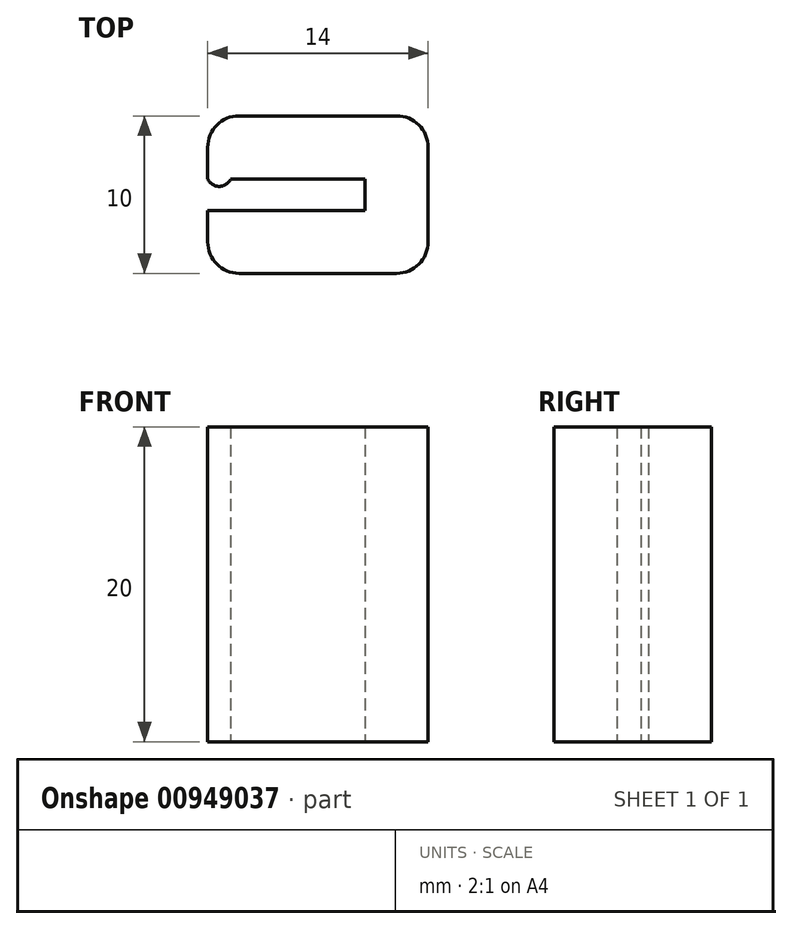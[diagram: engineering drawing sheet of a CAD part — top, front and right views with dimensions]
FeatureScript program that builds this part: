
annotation { "Feature Type Name" : "Feature", "Feature Type Description" : "" }
export const myFeature = defineFeature(function(context is Context, id is Id, definition is map)
    precondition{}
    {
        {
            var Q0;
            Q0=qCreatedBy(makeId("Top.planeOp"),FACE);
            var sketch = newSketch(context, id + "F0", { "sketchPlane" : qUnion([Q0])});
            skLineSegment(sketch, "E0.bottom", {"start": v(5, 1) * mm, "end": v(-5, 1) * mm});
            skLineSegment(sketch, "E0.top", {"start": v(5, -1) * mm, "end": v(-5, -1) * mm});
            skLineSegment(sketch, "E0.left", {"start": v(5, 1) * mm, "end": v(5, -1) * mm});
            skPoint(sketch, "E0.middle", {"position": v(0, 0) * mm});
            skLineSegment(sketch, "E1.bottom", {"start": v(-5, 1) * mm, "end": v(5, 1) * mm});
            skLineSegment(sketch, "E1.top", {"start": v(-5, 5) * mm, "end": v(5, 5) * mm});
            skLineSegment(sketch, "E1.left", {"start": v(-5, 1) * mm, "end": v(-5, 5) * mm});
            skLineSegment(sketch, "E1.right", {"start": v(5, 1) * mm, "end": v(5, 5) * mm});
            skLineSegment(sketch, "E2.top", {"start": v(5, -5) * mm, "end": v(-5, -5) * mm});
            skLineSegment(sketch, "E2.left", {"start": v(5, -1) * mm, "end": v(5, -5) * mm});
            skLineSegment(sketch, "E2.right", {"start": v(-5, -1) * mm, "end": v(-5, -5) * mm});
            skLineSegment(sketch, "E3.bottom", {"start": v(5, 5) * mm, "end": v(9, 5) * mm});
            skLineSegment(sketch, "E3.top", {"start": v(5, -5) * mm, "end": v(9, -5) * mm});
            skLineSegment(sketch, "E3.left", {"start": v(5, 5) * mm, "end": v(5, -5) * mm});
            skLineSegment(sketch, "E3.right", {"start": v(9, 5) * mm, "end": v(9, -5) * mm});
            skArc(sketch, "E4", {"start": v(-5, 1) * mm, "mid": v(-4.27, 0.52) * mm, "end": v(-3.53, 1) * mm});
            skLineSegment(sketch, "E5", {"start": v(0, 0) * mm, "end": v(-27.66, 0) * mm, "construction": true});
            skArc(sketch, "E6.MirrorCS", {"start": v(-5, -1) * mm, "mid": v(-4.27, -0.52) * mm, "end": v(-3.53, -1) * mm});
            skSolve(sketch);
        }
        {
            var Q0;
            Q0=makeQuery(id+"F0.imprint","IMPRINT",FACE,{"disambiguationData":[TD([[makeQuery(id+"F0.imprint","IMPRINT",EDGE,{"derivedFrom":sQuery(id+"F0.wireOp",EDGE,"E0.left")}),1.0]])]});
            var Q1;
            Q1=makeQuery(id+"F0.imprint","IMPRINT",FACE,{"disambiguationData":[TD([[makeQuery(id+"F0.imprint","IMPRINT",EDGE,{"derivedFrom":sQuery(id+"F0.wireOp",EDGE,"E1.top")}),-1.0]])]});
            var Q2;
            Q2=makeQuery(id+"F0.imprint","IMPRINT",FACE,{"disambiguationData":[TD([[makeQuery(id+"F0.imprint","IMPRINT",EDGE,{"derivedFrom":sQuery(id+"F0.wireOp",EDGE,"E2.top")}),-1.0]])]});
            var Q3;
            {var subQ0=sQuery(id+"F0.wireOp",EDGE,"E6.MirrorCS");Q3=makeQuery(id+"F0.imprint","IMPRINT",FACE,{"disambiguationData":[TD([[makeQuery(id+"F0.imprint","IMPRINT",EDGE,{"derivedFrom":subQ0}),-1.0]])]});}
            var Q4;
            {var subQ0=sQuery(id+"F0.wireOp",EDGE,"E4");Q4=makeQuery(id+"F0.imprint","IMPRINT",FACE,{"disambiguationData":[TD([[makeQuery(id+"F0.imprint","IMPRINT",EDGE,{"derivedFrom":subQ0}),1.0]])]});}
            extrude(context, id + "F1", {"entities" : qUnion([Q0, Q1, Q2, Q3, Q4]), "depth" : 20 * mm, "offsetDistance" : 25 * mm});
        }
        {
            var Q0;
            Q0=makeQuery(id+"F1.opExtrude","SWEPT_EDGE",EDGE,{"disambiguationData":[OSD([sQuery(id+"F0.wireOp",EDGE,"E3.bottom"),sQuery(id+"F0.wireOp",EDGE,"E3.right")])]});
            var Q1;
            Q1=makeQuery(id+"F1.opExtrude","SWEPT_EDGE",EDGE,{"disambiguationData":[OSD([sQuery(id+"F0.wireOp",EDGE,"E3.top"),sQuery(id+"F0.wireOp",EDGE,"E3.right")])]});
            var Q2;
            Q2=makeQuery(id+"F1.opExtrude","SWEPT_EDGE",EDGE,{"disambiguationData":[OSD([sQuery(id+"F0.wireOp",EDGE,"E2.top"),sQuery(id+"F0.wireOp",EDGE,"E2.right")])]});
            var Q3;
            Q3=makeQuery(id+"F1.opExtrude","SWEPT_EDGE",EDGE,{"disambiguationData":[OSD([sQuery(id+"F0.wireOp",EDGE,"E1.top"),sQuery(id+"F0.wireOp",EDGE,"E1.left")])]});
            fillet(context, id + "F2", {"entities" : qUnion([Q0, Q1, Q2, Q3]), "tangentPropagation" : true, "radius" : 2 * mm, "defaultsChanged" : false, "vertexSettings" : [], "allowEdgeOverflow" : false});
        }
    });
